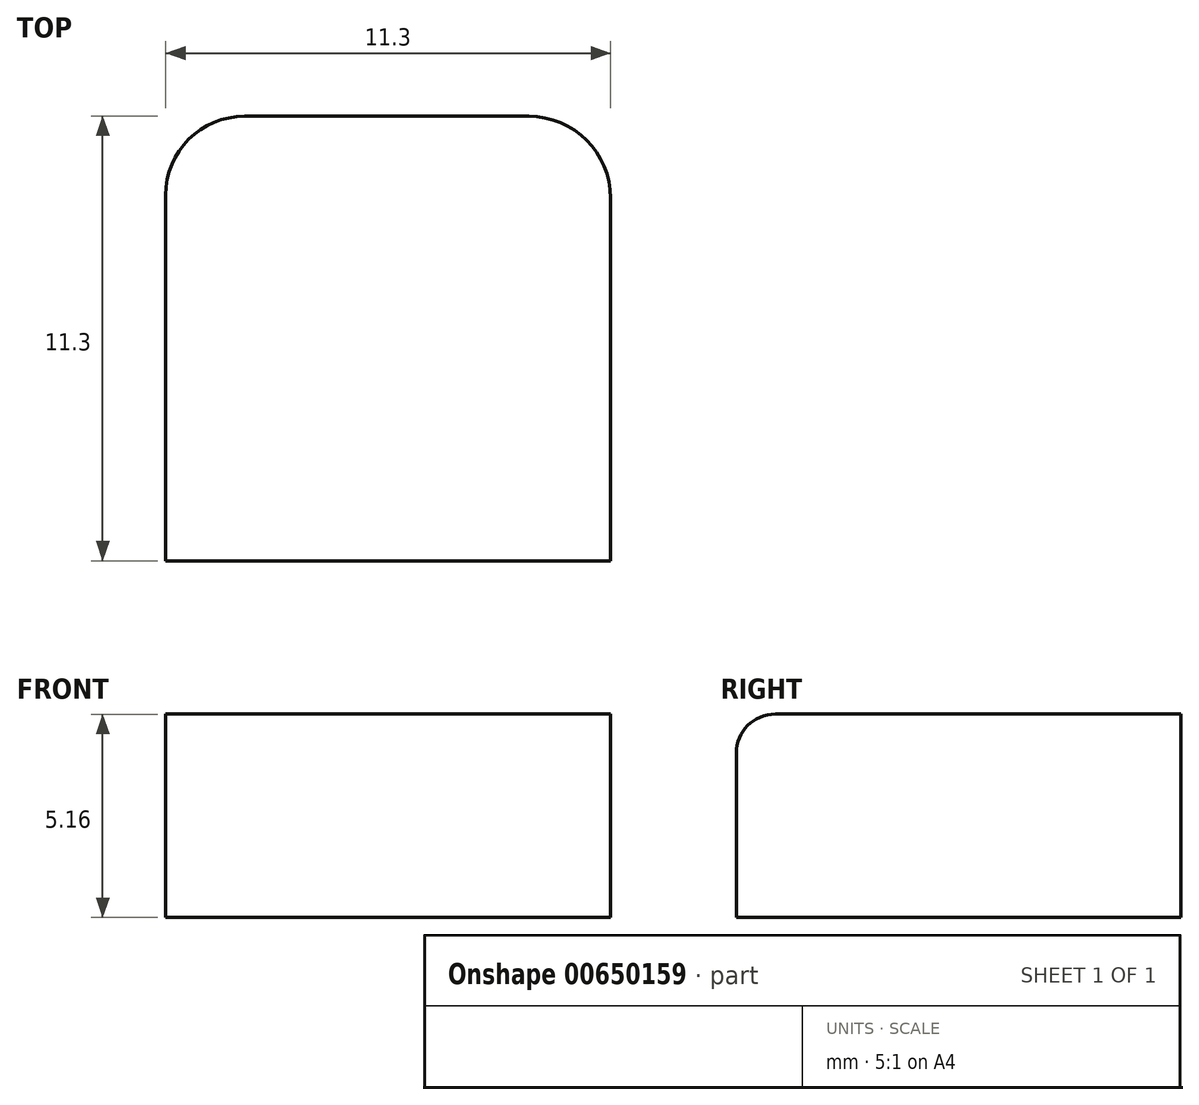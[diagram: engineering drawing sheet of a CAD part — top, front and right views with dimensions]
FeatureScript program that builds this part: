
annotation { "Feature Type Name" : "Feature", "Feature Type Description" : "" }
export const myFeature = defineFeature(function(context is Context, id is Id, definition is map)
    precondition{}
    {
        {
            var Q0;
            Q0=qCreatedBy(makeId("Top.planeOp"),FACE);
            var sketch = newSketch(context, id + "F0", { "sketchPlane" : qUnion([Q0])});
            skLineSegment(sketch, "E0.bottom", {"start": v(0, 0) * mm, "end": v(11.3, 0) * mm});
            skLineSegment(sketch, "E0.top", {"start": v(0, 16.4) * mm, "end": v(11.3, 16.4) * mm});
            skLineSegment(sketch, "E0.left", {"start": v(0, 0) * mm, "end": v(0, 16.4) * mm});
            skLineSegment(sketch, "E0.right", {"start": v(11.3, 0) * mm, "end": v(11.3, 16.4) * mm});
            skSolve(sketch);
        }
        {
            var Q0;
            Q0=makeQuery(id+"F0.imprint","IMPRINT",FACE,{"disambiguationData":[TD([[makeQuery(id+"F0.imprint","IMPRINT",EDGE,{"derivedFrom":sQuery(id+"F0.wireOp",EDGE,"E0.bottom")}),1.0]])]});
            extrude(context, id + "F1", {"entities" : qUnion([Q0]), "depth" : 11.3 * mm, "offsetDistance" : 25 * mm});
        }
        {
            var Q0;
            Q0=makeQuery(id+"F1.opExtrude","CAP_FACE",FACE,{"disambiguationData":[OSD([sQuery(id+"F0.wireOp",EDGE,"E0.bottom"),sQuery(id+"F0.wireOp",EDGE,"E0.top"),sQuery(id+"F0.wireOp",EDGE,"E0.left"),sQuery(id+"F0.wireOp",EDGE,"E0.right")])],"isStart":false});
            var sketch = newSketch(context, id + "F2", { "sketchPlane" : qUnion([Q0])});
            skLineSegment(sketch, "E1.bottom", {"start": v(0, 0) * mm, "end": v(11.3, 0) * mm});
            skLineSegment(sketch, "E1.top", {"start": v(0, 11.24) * mm, "end": v(11.3, 11.24) * mm});
            skLineSegment(sketch, "E1.left", {"start": v(0, 0) * mm, "end": v(0, 11.24) * mm});
            skLineSegment(sketch, "E1.right", {"start": v(11.3, 0) * mm, "end": v(11.3, 11.24) * mm});
            skSolve(sketch);
        }
        {
            var Q0;
            Q0=makeQuery(id+"F2.imprint","IMPRINT",FACE,{"disambiguationData":[TD([[makeQuery(id+"F2.imprint","IMPRINT",EDGE,{"derivedFrom":sQuery(id+"F2.wireOp",EDGE,"E1.bottom")}),1.0]])]});
            extrude(context, id + "F3", {"entities" : qUnion([Q0]), "operationType" : NewBodyOperationType.REMOVE, "oppositeDirection" : true, "depth" : 25 * mm, "offsetDistance" : 25 * mm});
        }
        {
            var Q0;
            Q0=makeQuery(id+"F1.opExtrude","CAP_EDGE",EDGE,{"disambiguationData":[OSD([sQuery(id+"F0.wireOp",EDGE,"E0.top")])],"isStart":false});
            fillet(context, id + "F4", {"entities" : qUnion([Q0]), "radius" : 0.99 * mm, "tangentPropagation" : true, "allowEdgeOverflow" : false});
        }
        {
            var Q0;
            Q0=makeQuery(id+"F1.opExtrude","CAP_EDGE",EDGE,{"disambiguationData":[OSD([sQuery(id+"F0.wireOp",EDGE,"E0.right")])],"isStart":true});
            fillet(context, id + "F5", {"entities" : qUnion([Q0]), "radius" : 2.08 * mm, "tangentPropagation" : true, "allowEdgeOverflow" : false});
        }
        {
            var Q0;
            Q0=makeQuery(id+"F1.opExtrude","CAP_EDGE",EDGE,{"disambiguationData":[OSD([sQuery(id+"F0.wireOp",EDGE,"E0.left")])],"isStart":true});
            fillet(context, id + "F6", {"entities" : qUnion([Q0]), "radius" : 2 * mm, "tangentPropagation" : true, "allowEdgeOverflow" : false});
        }
        {
            var Q0;
            Q0=makeQuery(id+"F1.opExtrude","SWEPT_BODY",BODY,{"disambiguationData":[OSD([sQuery(id+"F0.wireOp",EDGE,"E0.bottom"),sQuery(id+"F0.wireOp",EDGE,"E0.top"),sQuery(id+"F0.wireOp",EDGE,"E0.left"),sQuery(id+"F0.wireOp",EDGE,"E0.right")])]});
            var Q1;
            Q1=makeQuery(id+"F3.boolean.opBoolean","INTERSECT",EDGE,{"derivedFrom":[makeQuery(id+"F1.opExtrude","CAP_FACE",FACE,{"disambiguationData":[OSD([sQuery(id+"F0.wireOp",EDGE,"E0.bottom"),sQuery(id+"F0.wireOp",EDGE,"E0.top"),sQuery(id+"F0.wireOp",EDGE,"E0.left"),sQuery(id+"F0.wireOp",EDGE,"E0.right")])],"isStart":true}),makeQuery(id+"F3.opExtrude","SWEPT_FACE",FACE,{"disambiguationData":[OSD([sQuery(id+"F2.wireOp",EDGE,"E1.top")])]})]});
            transform(context, id + "F7", {"entities" : qUnion([Q0]), "transformType" : TransformType.ROTATION, "transformAxis" : qUnion([Q1]), "angle" : 90 * degree, "makeCopy" : false});
        }
    });
